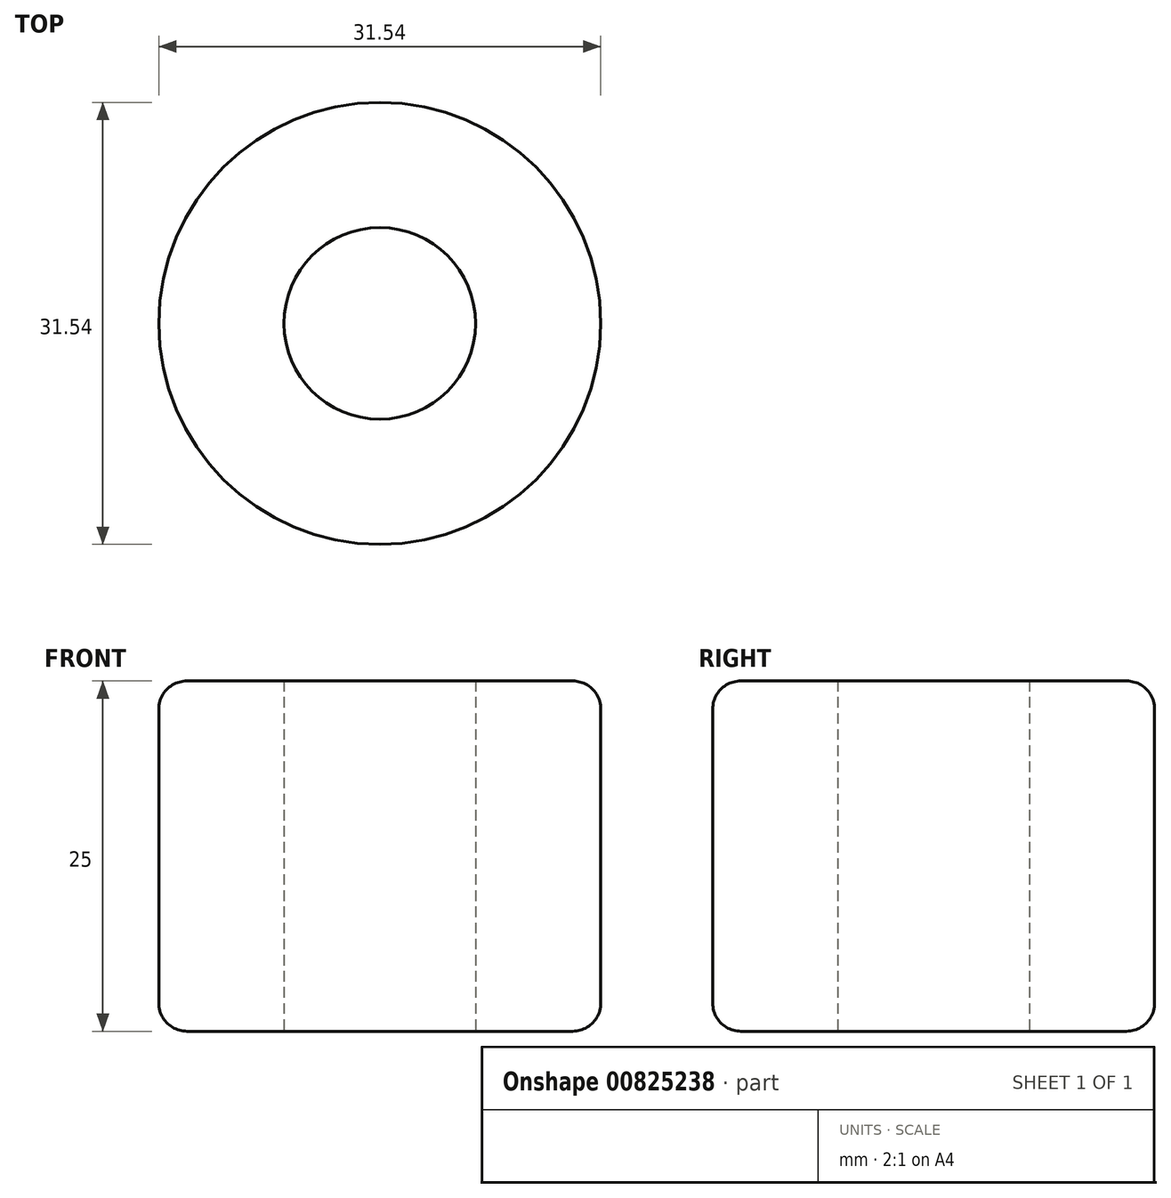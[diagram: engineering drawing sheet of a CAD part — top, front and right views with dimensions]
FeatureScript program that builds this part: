
annotation { "Feature Type Name" : "Feature", "Feature Type Description" : "" }
export const myFeature = defineFeature(function(context is Context, id is Id, definition is map)
    precondition{}
    {
        {
            var Q0;
            Q0=qCreatedBy(makeId("Top.planeOp"),FACE);
            var sketch = newSketch(context, id + "F0", { "sketchPlane" : qUnion([Q0])});
            skCircle(sketch, "E0", {"center": v(-22.66, -18.11) * mm, "radius": 15.77 * mm});
            skSolve(sketch);
        }
        {
            var Q0;
            Q0 = qSketchRegion(id + "F0", true);
            extrude(context, id + "F1", {"entities" : qUnion([Q0]), "depth" : 25 * mm, "offsetDistance" : 25 * mm});
        }
        {
            var Q0;
            Q0=makeQuery(id+"F1.opExtrude","SWEPT_EDGE",EDGE,{"disambiguationData":[OSD([sQuery(id+"F0.wireOp",EDGE,"nzMMtbA8-R8CW-zkJL-nHtR-wrthLNUB78wq.top"),sQuery(id+"F0.wireOp",EDGE,"nzMMtbA8-R8CW-zkJL-nHtR-wrthLNUB78wq.right")])]});
            var Q1;
            Q1=makeQuery(id+"F1.opExtrude","SWEPT_EDGE",EDGE,{"disambiguationData":[OSD([sQuery(id+"F0.wireOp",EDGE,"nzMMtbA8-R8CW-zkJL-nHtR-wrthLNUB78wq.top"),sQuery(id+"F0.wireOp",EDGE,"nzMMtbA8-R8CW-zkJL-nHtR-wrthLNUB78wq.left")])]});
            var Q2;
            Q2=makeQuery(id+"F1.opExtrude","SWEPT_EDGE",EDGE,{"disambiguationData":[OSD([sQuery(id+"F0.wireOp",EDGE,"nzMMtbA8-R8CW-zkJL-nHtR-wrthLNUB78wq.bottom"),sQuery(id+"F0.wireOp",EDGE,"nzMMtbA8-R8CW-zkJL-nHtR-wrthLNUB78wq.right")])]});
            var Q3;
            Q3=makeQuery(id+"F1.opExtrude","CAP_EDGE",EDGE,{"disambiguationData":[OSD([sQuery(id+"F0.wireOp",EDGE,"E0")])],"isStart":true});
            var Q4;
            Q4=makeQuery(id+"F1.opExtrude","CAP_EDGE",EDGE,{"disambiguationData":[OSD([sQuery(id+"F0.wireOp",EDGE,"E0")])],"isStart":false});
            var Q5;
            Q5=makeQuery(id+"F1.opExtrude","SWEPT_EDGE",EDGE,{"disambiguationData":[OSD([sQuery(id+"F0.wireOp",EDGE,"nzMMtbA8-R8CW-zkJL-nHtR-wrthLNUB78wq.bottom"),sQuery(id+"F0.wireOp",EDGE,"nzMMtbA8-R8CW-zkJL-nHtR-wrthLNUB78wq.left")])]});
            fillet(context, id + "F2", {"entities" : qUnion([Q0, Q1, Q2, Q3, Q4, Q5]), "radius" : 2 * mm, "tangentPropagation" : true, "allowEdgeOverflow" : false});
        }
        {
            var Q0;
            Q0=makeQuery(id+"F1.opExtrude","CAP_FACE",FACE,{"disambiguationData":[OSD([sQuery(id+"F0.wireOp",EDGE,"E0")])],"isStart":true});
            var sketch = newSketch(context, id + "F3", { "sketchPlane" : qUnion([Q0])});
            skCircle(sketch, "E1", {"center": v(-22.66, 18.11) * mm, "radius": 6.83 * mm});
            skSolve(sketch);
        }
        {
            var Q0;
            Q0 = qSketchRegion(id + "F3", true);
            extrude(context, id + "F4", {"entities" : qUnion([Q0]), "operationType" : NewBodyOperationType.REMOVE, "oppositeDirection" : true, "depth" : 40 * mm, "offsetDistance" : 25 * mm});
        }
    });
